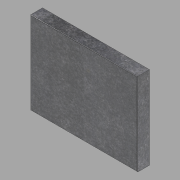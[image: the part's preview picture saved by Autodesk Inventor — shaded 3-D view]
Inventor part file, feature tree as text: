
AUTODESK INVENTOR PART (.ipt)
format: ipt  version: 2022.1 (Build 261234020, 234B)  size: 108,544 bytes
history: native  units: in
note: dims shown in document units (in); Inventor stores cm internally (conversion verified against a paired STEP export)
features: extrude x1, fillet x1, sketch x1
ambient origin geometry x8: Origin, YZ Plane, XZ Plane, XY Plane, X Axis, Y Axis, Z Axis, Center Point
bodies: Solid1 (feature_tree)
feature tree (3):
  extrude  "Extrusion1"  Depth=41.0in
  fillet  "Fillet1"  Radius=6.0in
  sketch  "Sketch1"  dims[d0=53.0in d1=41.0in d2=6.0in d3=0.0in d4=0.25in]
